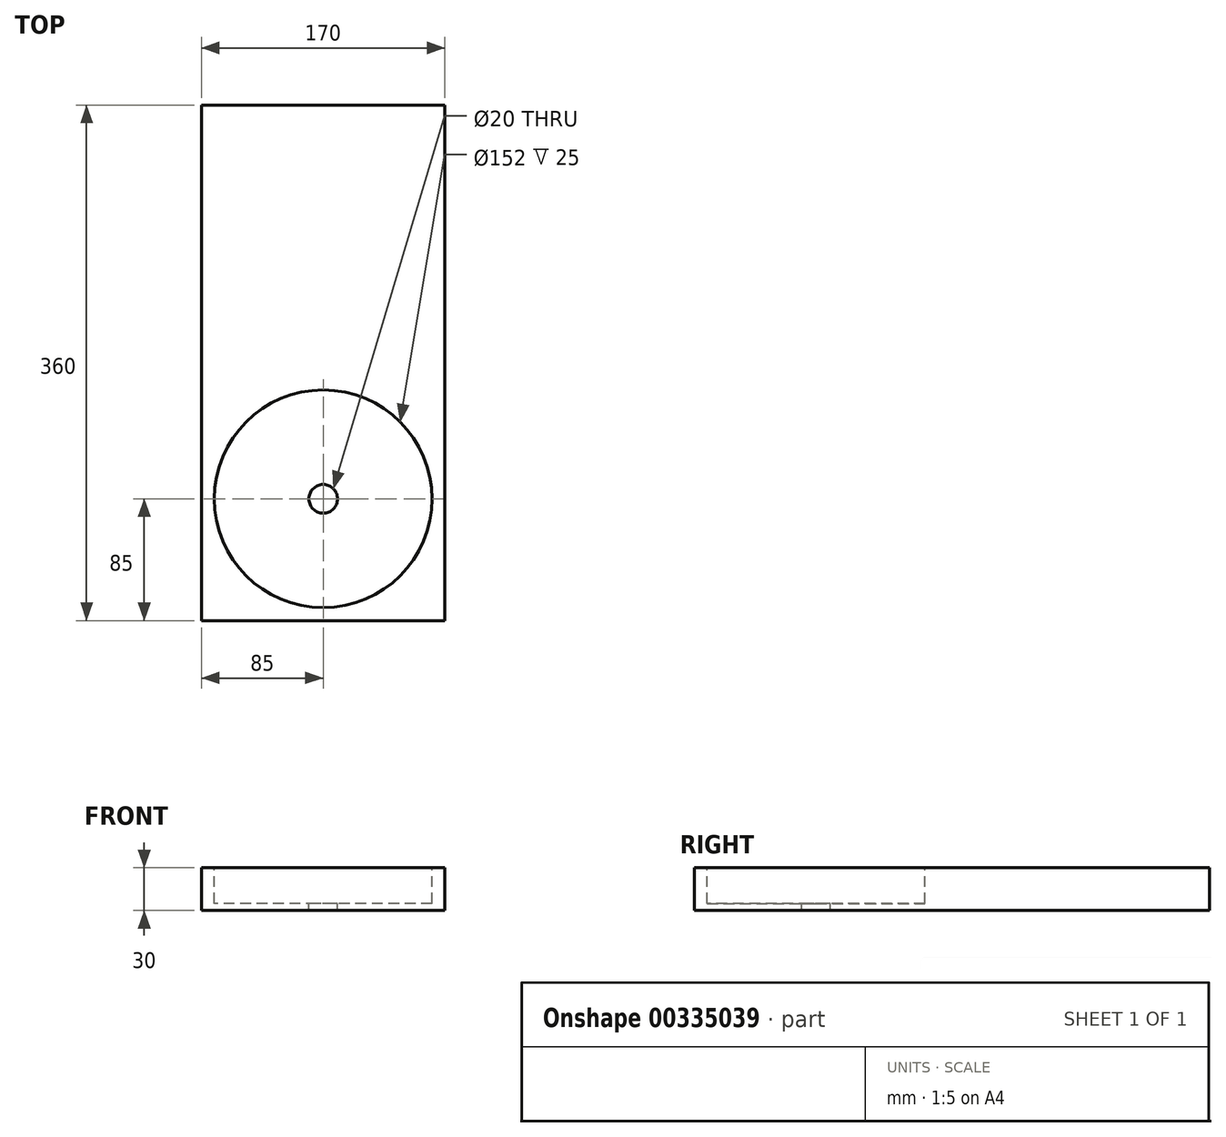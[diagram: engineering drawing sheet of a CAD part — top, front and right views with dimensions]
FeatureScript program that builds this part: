
annotation { "Feature Type Name" : "Feature", "Feature Type Description" : "" }
export const myFeature = defineFeature(function(context is Context, id is Id, definition is map)
    precondition{}
    {
        {
            var Q0;
            Q0=qCreatedBy(makeId("Top.planeOp"),FACE);
            var sketch = newSketch(context, id + "F0", { "sketchPlane" : qUnion([Q0])});
            skLineSegment(sketch, "E0.bottom", {"start": v(85, -180) * mm, "end": v(-85, -180) * mm});
            skLineSegment(sketch, "E0.top", {"start": v(85, 180) * mm, "end": v(-85, 180) * mm});
            skLineSegment(sketch, "E0.left", {"start": v(85, -180) * mm, "end": v(85, 180) * mm});
            skLineSegment(sketch, "E0.right", {"start": v(-85, -180) * mm, "end": v(-85, 180) * mm});
            skPoint(sketch, "E0.middle", {"position": v(0, 0) * mm});
            skSolve(sketch);
        }
        {
            var Q0;
            Q0=makeQuery(id+"F0.imprint","IMPRINT",FACE,{"disambiguationData":[TD([[makeQuery(id+"F0.imprint","IMPRINT",EDGE,{"derivedFrom":sQuery(id+"F0.wireOp",EDGE,"E0.bottom")}),-1.0]])]});
            extrude(context, id + "F1", {"entities" : qUnion([Q0]), "depth" : 30 * mm});
        }
        {
            var Q0;
            Q0=makeQuery(id+"F1.opExtrude","CAP_FACE",FACE,{"disambiguationData":[OSD([sQuery(id+"F0.wireOp",EDGE,"E0.bottom"),sQuery(id+"F0.wireOp",EDGE,"E0.top"),sQuery(id+"F0.wireOp",EDGE,"E0.left"),sQuery(id+"F0.wireOp",EDGE,"E0.right")])],"isStart":false});
            var sketch = newSketch(context, id + "F2", { "sketchPlane" : qUnion([Q0])});
            skCircle(sketch, "E1", {"center": v(0, -95) * mm, "radius": 10 * mm});
            skSolve(sketch);
        }
        {
            var Q0;
            Q0=makeQuery(id+"F2.imprint","IMPRINT",FACE,{"disambiguationData":[TD([[makeQuery(id+"F2.imprint","IMPRINT",EDGE,{"derivedFrom":sQuery(id+"F2.wireOp",EDGE,"E1")}),1.0]])]});
            extrude(context, id + "F3", {"entities" : qUnion([Q0]), "operationType" : NewBodyOperationType.REMOVE, "endBound" : BoundingType.THROUGH_ALL, "oppositeDirection" : true, "depth" : 25 * mm});
        }
        {
            var Q0;
            Q0=makeQuery(id+"F1.opExtrude","CAP_FACE",FACE,{"disambiguationData":[OSD([sQuery(id+"F0.wireOp",EDGE,"E0.bottom"),sQuery(id+"F0.wireOp",EDGE,"E0.top"),sQuery(id+"F0.wireOp",EDGE,"E0.left"),sQuery(id+"F0.wireOp",EDGE,"E0.right")])],"isStart":false});
            var sketch = newSketch(context, id + "F4", { "sketchPlane" : qUnion([Q0])});
            skCircle(sketch, "E2", {"center": v(0, -95) * mm, "radius": 76 * mm});
            skSolve(sketch);
        }
        {
            var Q0;
            Q0 = qSketchRegion(id + "F4", true);
            var Q1;
            Q1=makeQuery(id+"F4.imprint","IMPRINT",FACE,{"disambiguationData":[TD([[makeQuery(id+"F4.imprint","IMPRINT",EDGE,{"derivedFrom":sQuery(id+"F4.wireOp",EDGE,"E2")}),1.0]])]});
            extrude(context, id + "F5", {"entities" : qUnion([Q0, Q1]), "operationType" : NewBodyOperationType.REMOVE, "oppositeDirection" : true, "depth" : 25 * mm});
        }
    });
